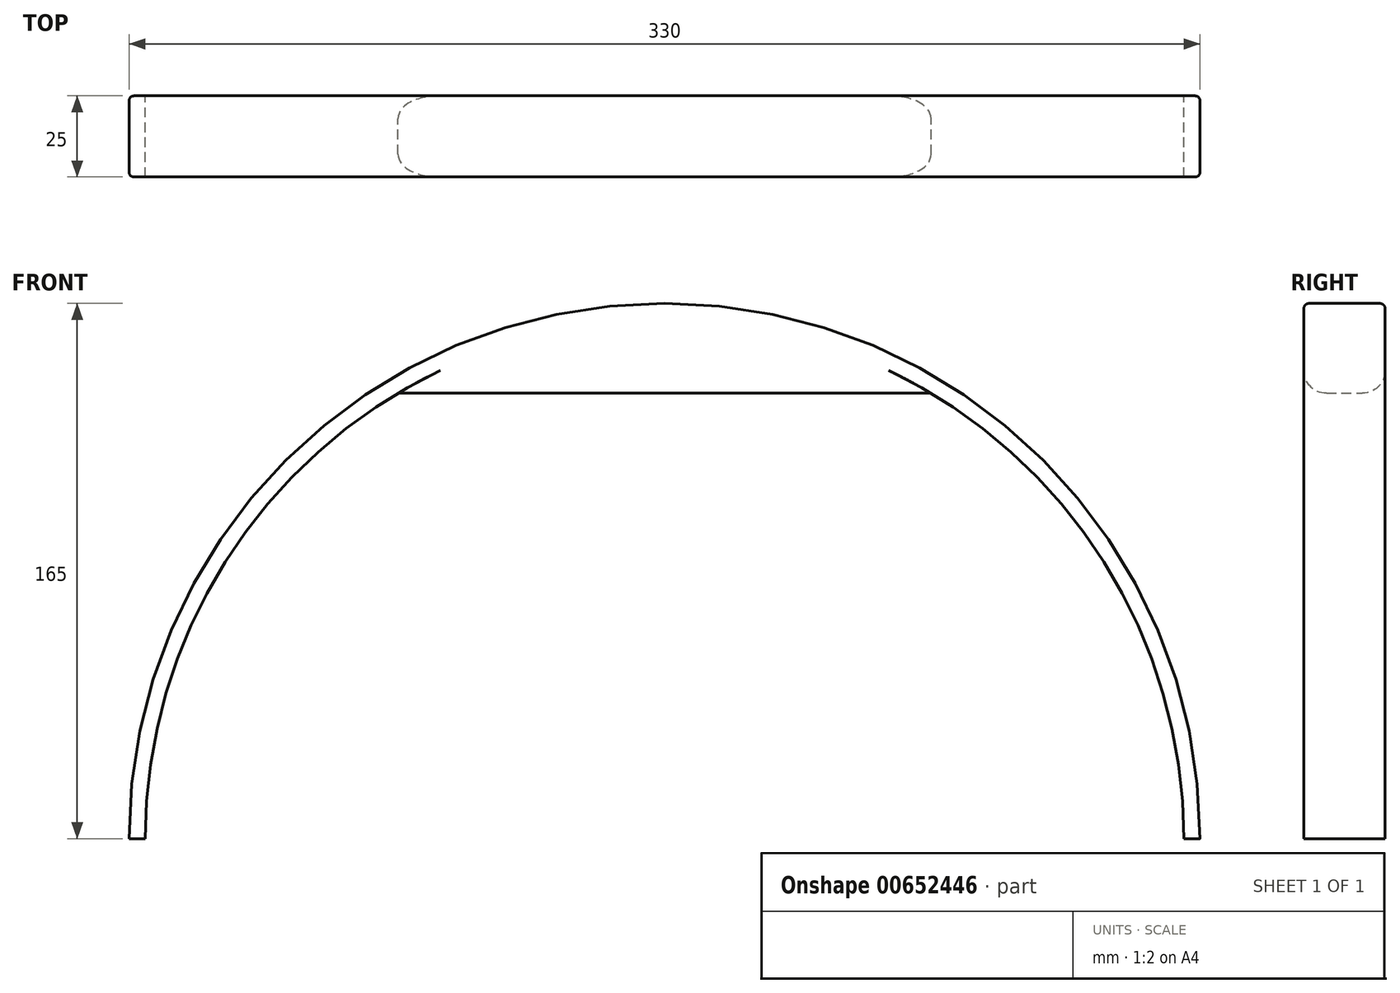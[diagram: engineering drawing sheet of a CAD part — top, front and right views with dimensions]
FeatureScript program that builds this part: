
annotation { "Feature Type Name" : "Feature", "Feature Type Description" : "" }
export const myFeature = defineFeature(function(context is Context, id is Id, definition is map)
    precondition{}
    {
        {
            var Q0;
            Q0=qCreatedBy(makeId("Front.planeOp"),FACE);
            var sketch = newSketch(context, id + "F0", { "sketchPlane" : qUnion([Q0])});
            skArc(sketch, "E0", {"start": v(-165, 0) * mm, "mid": v(0, 165) * mm, "end": v(165, 0) * mm});
            skArc(sketch, "E1", {"start": v(-160, 0) * mm, "mid": v(0, 160) * mm, "end": v(160, 0) * mm});
            skLineSegment(sketch, "E2", {"start": v(-165, 0) * mm, "end": v(-160, 0) * mm});
            skLineSegment(sketch, "E3", {"start": v(160, 0) * mm, "end": v(165, 0) * mm});
            skLineSegment(sketch, "E4", {"start": v(-82.12, 137.32) * mm, "end": v(82.12, 137.32) * mm});
            skSolve(sketch);
        }
        {
            var Q0;
            Q0 = qSketchRegion(id + "F0", true);
            extrude(context, id + "F1", {"entities" : qUnion([Q0]), "depth" : 25 * mm, "offsetDistance" : 25 * mm});
        }
        {
            var Q0;
            {var subQ0=sQuery(id+"F0.wireOp",EDGE,"E1");Q0=makeQuery(id+"F1.opExtrude","CAP_EDGE",EDGE,{"disambiguationData":[OSD([subQ0]),TDD([makeQuery(id+"F0.imprint","IMPRINT",EDGE,{"disambiguationData":[TD([[makeQuery(id+"F0.imprint","INTERSECT",VERTEX,{"derivedFrom":[subQ0,sQuery(id+"F0.wireOp",EDGE,"E3")]}),1.0]])],"derivedFrom":subQ0})])],"isStart":true});}
            var Q1;
            Q1=makeQuery(id+"F1.opExtrude","CAP_EDGE",EDGE,{"disambiguationData":[OSD([sQuery(id+"F0.wireOp",EDGE,"E0")])],"isStart":true});
            var Q2;
            {var subQ0=sQuery(id+"F0.wireOp",EDGE,"E1");Q2=makeQuery(id+"F1.opExtrude","CAP_EDGE",EDGE,{"disambiguationData":[OSD([subQ0]),TDD([makeQuery(id+"F0.imprint","IMPRINT",EDGE,{"disambiguationData":[TD([[makeQuery(id+"F0.imprint","INTERSECT",VERTEX,{"derivedFrom":[subQ0,sQuery(id+"F0.wireOp",EDGE,"E2")]}),-1.0]])],"derivedFrom":subQ0})])],"isStart":true});}
            var Q3;
            Q3=makeQuery(id+"F1.opExtrude","CAP_EDGE",EDGE,{"disambiguationData":[OSD([sQuery(id+"F0.wireOp",EDGE,"E0")])],"isStart":false});
            var Q4;
            {var subQ0=sQuery(id+"F0.wireOp",EDGE,"E1");Q4=makeQuery(id+"F1.opExtrude","CAP_EDGE",EDGE,{"disambiguationData":[OSD([subQ0]),TDD([makeQuery(id+"F0.imprint","IMPRINT",EDGE,{"disambiguationData":[TD([[makeQuery(id+"F0.imprint","INTERSECT",VERTEX,{"derivedFrom":[subQ0,sQuery(id+"F0.wireOp",EDGE,"E2")]}),-1.0]])],"derivedFrom":subQ0})])],"isStart":false});}
            var Q5;
            {var subQ0=sQuery(id+"F0.wireOp",EDGE,"E1");Q5=makeQuery(id+"F1.opExtrude","CAP_EDGE",EDGE,{"disambiguationData":[OSD([subQ0]),TDD([makeQuery(id+"F0.imprint","IMPRINT",EDGE,{"disambiguationData":[TD([[makeQuery(id+"F0.imprint","INTERSECT",VERTEX,{"derivedFrom":[subQ0,sQuery(id+"F0.wireOp",EDGE,"E3")]}),1.0]])],"derivedFrom":subQ0})])],"isStart":false});}
            fillet(context, id + "F2", {"entities" : qUnion([Q0, Q1, Q2, Q3, Q4, Q5]), "radius" : 1.5 * mm, "tangentPropagation" : true, "allowEdgeOverflow" : false});
        }
        {
            var Q0;
            Q0=makeQuery(id+"F1.opExtrude","CAP_EDGE",EDGE,{"disambiguationData":[OSD([sQuery(id+"F0.wireOp",EDGE,"E4")])],"isStart":false});
            var Q1;
            Q1=makeQuery(id+"F1.opExtrude","CAP_EDGE",EDGE,{"disambiguationData":[OSD([sQuery(id+"F0.wireOp",EDGE,"E4")])],"isStart":true});
            fillet(context, id + "F3", {"entities" : qUnion([Q0, Q1]), "radius" : 7 * mm, "tangentPropagation" : true, "allowEdgeOverflow" : false});
        }
    });
